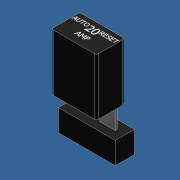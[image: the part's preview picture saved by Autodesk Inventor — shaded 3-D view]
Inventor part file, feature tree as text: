
AUTODESK INVENTOR PART (.ipt)
format: ipt  version: unknown  size: 424,960 bytes
history: native  units: mm (DEFAULTED — no unit token found)
features: extrude x4, sketch x4, plane x3
ambient origin geometry x5: Origin, X Axis, Y Axis, Z Axis, Center Point
feature tree (11):
  extrude  "Extrusion1"  Depth=9.906mm
  extrude  "Extrusion2"  Depth=19.812mm TaperAngle=0.0deg
  extrude  "Extrusion3"  Depth=5.3848mm
  extrude  "Extrusion4"  Depth=2.9718mm
  plane  "YZ Plane (RIGHT)"
  plane  "XZ Plane (TOP)"
  plane  "XY Plane (FRONT)"
  sketch  "Sketch2"  dims[d0=15.748mm d1=9.906mm]
  sketch  "Sketch3"  dims[d2=0.762mm d3=19.812mm d4=0.0mm]
  sketch  "Sketch4"  dims[d5=0.7112mm d6=5.3848mm]
  sketch  "Sketch5"  dims[d7=7.874mm d8=2.9718mm d9=14.478mm d10=0.0mm d11=34.6964mm d12=6.7056mm d13=7.62mm d14=19.812mm d15=0.0mm d16=0.00254mm d17=0.0mm]
